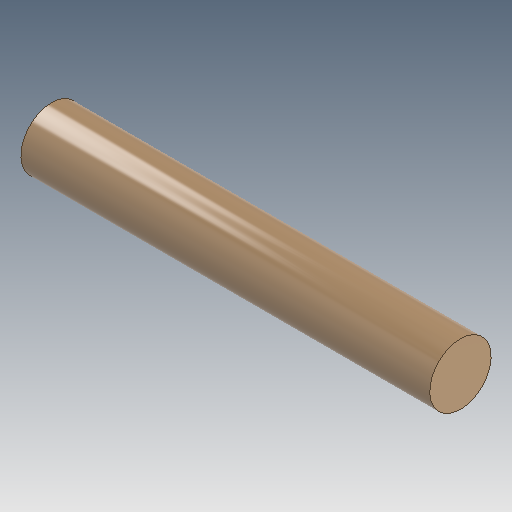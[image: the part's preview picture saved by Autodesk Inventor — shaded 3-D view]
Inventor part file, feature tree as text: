
AUTODESK INVENTOR PART (.ipt)
format: ipt  version: 2017 (Build 210142000, 142)  size: 91,648 bytes
history: native  units: mm
features: extrude x1, sketch x1
ambient origin geometry x8: Origin, YZ Plane, XZ Plane, XY Plane, X Axis, Y Axis, Z Axis, Center Point
bodies: Body1 (feature_tree)
feature tree (2):
  extrude  "Extrusion3"  Depth=20.0mm TaperAngle=0.0deg
  sketch  "Sketch3"  dims[d8=3.0mm d9=20.0mm d10=0.0mm]
